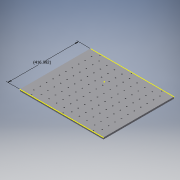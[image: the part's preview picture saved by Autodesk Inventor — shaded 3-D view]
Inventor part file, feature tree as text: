
AUTODESK INVENTOR PART (.ipt)
format: ipt  version: 2017 (Build 210142000, 142)  size: 274,944 bytes
history: native  units: in
note: dims shown in document units (in); Inventor stores cm internally (conversion verified against a paired STEP export)
features: sketch x10, extrude x8
ambient origin geometry x8: Origin, YZ Plane, XZ Plane, XY Plane, X Axis, Y Axis, Z Axis, Center Point
bodies: Solid1 (feature_tree)
feature tree (18):
  extrude  "Extrusion1"  Depth=16.4173in
  sketch  "Sketch3"  dims[d2=0.3937in d3=0.0in d4=16.417in]
  extrude  "Extrusion2"  Depth=16.417in
  extrude  "Extrusion3"  Depth=16.1417in
  extrude  "Extrusion4"  Depth=0.3937in TaperAngle=0.0deg
  extrude  "Extrusion5"  Depth=16.142in
  sketch  "Sketch8"  dims[d14=0.3937in d15=0.0in d16=0.25in]
  extrude  "Extrusion6"  Depth=9.6457in
  extrude  "Extrusion7"  Depth=0.3937in
  extrude  "Extrusion10"  Depth=16.9685in
  sketch  "Sketch1"  dims[d0=19.4488in d1=16.4173in]
  sketch  "Sketch4"  dims[d5=0.25in d6=16.1417in]
  sketch  "Sketch5"  dims[d7=2.5591in d8=0.3937in d9=0.0in]
  sketch  "Sketch6"  dims[d10=0.25in d11=16.142in]
  sketch  "Sketch7"  dims[d12=16.1417in d13=9.6457in]
  sketch  "Sketch9"  dims[d17=16.142in d18=16.9685in]
  sketch  "Sketch10"  dims[d19=0.5187in d20=0.0in]
  sketch  "Sketch15"  dims[d21=0.25in d22=2.5591in d23=16.142in d24=0.3937in d25=0.0in d26=0.25in d27=16.142in d28=9.6457in d29=0.3937in d30=0.0in d31=0.25in d32=16.142in d33=16.9685in d34=0.3937in d35=0.0in d130=0.2756in d131=1.4924in d132=1.7681in d133=3.937in d135=1.7681in d136=3.937in d138=1.4924in d143=0.3937in d144=0.0in]
